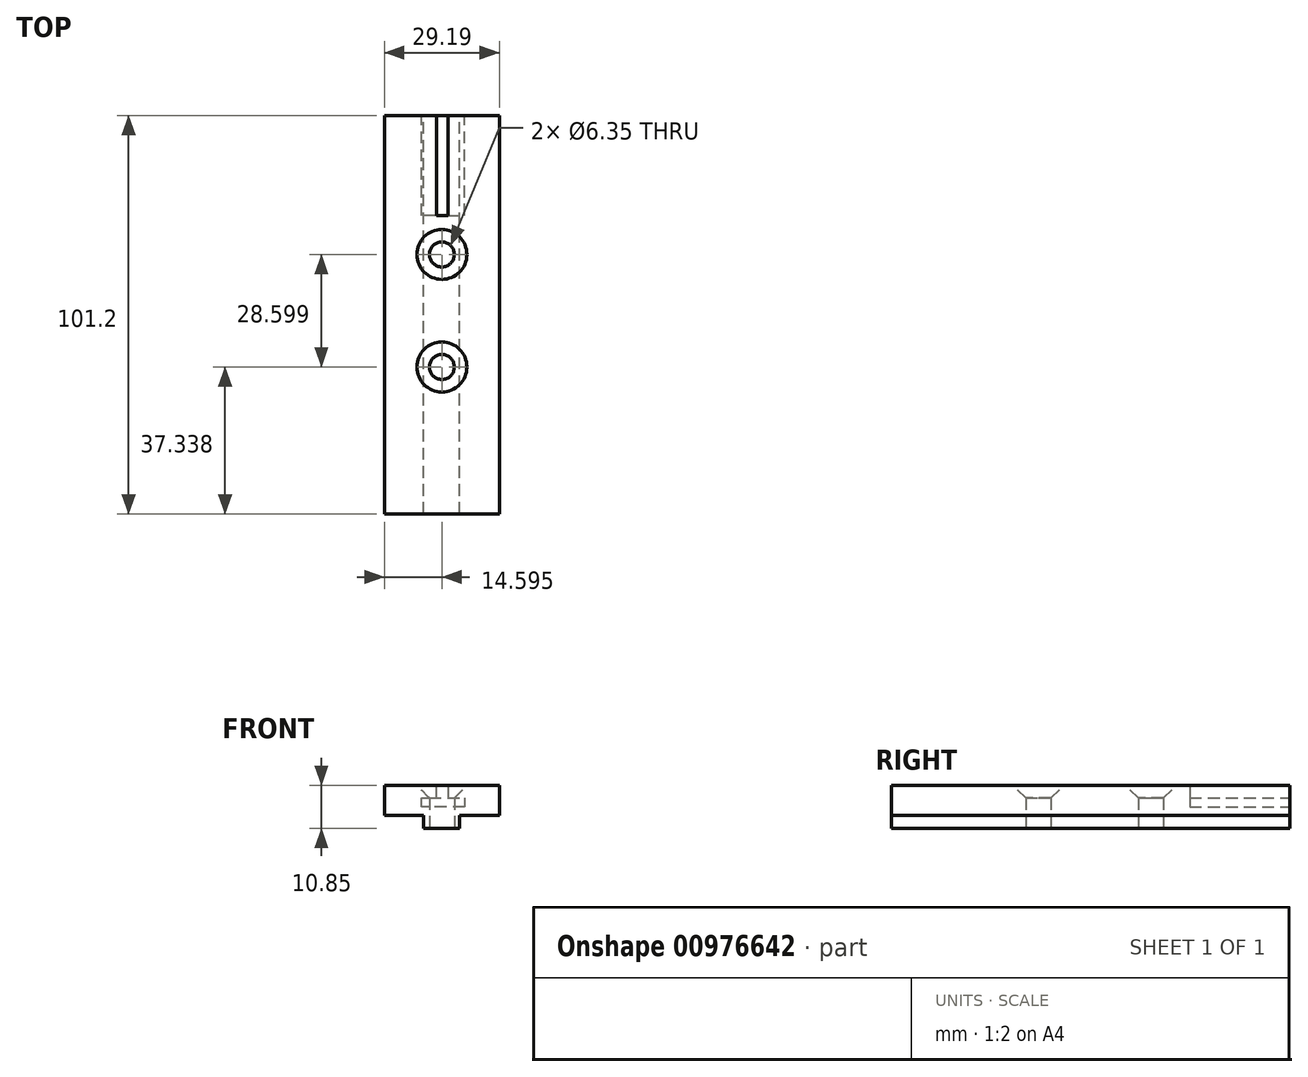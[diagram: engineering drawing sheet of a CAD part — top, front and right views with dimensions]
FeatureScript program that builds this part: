
annotation { "Feature Type Name" : "Feature", "Feature Type Description" : "" }
export const myFeature = defineFeature(function(context is Context, id is Id, definition is map)
    precondition{}
    {
        {
            var Q0;
            Q0=qCreatedBy(makeId("Front.planeOp"),FACE);
            var sketch = newSketch(context, id + "F0", { "sketchPlane" : qUnion([Q0])});
            skLineSegment(sketch, "E0", {"start": v(-1.19, 0) * mm, "end": v(29.2, 0) * mm});
            skLineSegment(sketch, "E1", {"start": v(29.2, 0) * mm, "end": v(29.2, -7.58) * mm});
            skLineSegment(sketch, "E2", {"start": v(29.2, -7.58) * mm, "end": v(18.01, -7.58) * mm});
            skLineSegment(sketch, "E3", {"start": v(18.01, -7.58) * mm, "end": v(18.01, -10.85) * mm});
            skLineSegment(sketch, "E4", {"start": v(18.01, -10.85) * mm, "end": v(12.2, -10.85) * mm});
            skLineSegment(sketch, "E5", {"start": v(12.2, -10.85) * mm, "end": v(12.2, -7.58) * mm});
            skLineSegment(sketch, "E6", {"start": v(12.2, -7.58) * mm, "end": v(0, -7.58) * mm});
            skLineSegment(sketch, "E7", {"start": v(0, -7.58) * mm, "end": v(0, 0) * mm});
            skSolve(sketch);
        }
        {
            var Q0;
            {var subQ0=sQuery(id+"F0.wireOp",EDGE,"E1");Q0=makeQuery(id+"F0.imprint","IMPRINT",FACE,{"disambiguationData":[TD([[makeQuery(id+"F0.imprint","IMPRINT",EDGE,{"derivedFrom":subQ0}),-1.0]])]});}
            extrude(context, id + "F1", {"entities" : qUnion([Q0]), "depth" : 25 * mm, "offsetDistance" : 25.4 * mm});
        }
        {
            var Q0;
            Q0=makeQuery(id+"F1.opExtrude","SWEPT_FACE",FACE,{"disambiguationData":[OSD([sQuery(id+"F0.wireOp",EDGE,"E5")])]});
            extrude(context, id + "F2", {"entities" : qUnion([Q0]), "operationType" : NewBodyOperationType.ADD, "depth" : 2.18 * mm, "offsetDistance" : 25.4 * mm});
        }
        {
            var Q0;
            {var subQ0=sQuery(id+"F0.wireOp",EDGE,"E5");Q0=makeQuery(id+"F2.boolean.opBoolean","MERGE",FACE,{"derivedFrom":[makeQuery(id+"F1.opExtrude","CAP_FACE",FACE,{"disambiguationData":[OSD([sQuery(id+"F0.wireOp",EDGE,"E0"),sQuery(id+"F0.wireOp",EDGE,"E1"),sQuery(id+"F0.wireOp",EDGE,"E2"),sQuery(id+"F0.wireOp",EDGE,"E3"),sQuery(id+"F0.wireOp",EDGE,"E4"),subQ0,sQuery(id+"F0.wireOp",EDGE,"E6"),sQuery(id+"F0.wireOp",EDGE,"E7")])],"isStart":true}),makeQuery(id+"F2.opExtrude","SWEPT_FACE",FACE,{"disambiguationData":[OSD([subQ0]),TDD([makeQuery(id+"F1.opExtrude","CAP_EDGE",EDGE,{"disambiguationData":[OSD([subQ0])],"isStart":true})])]})]});}
            extrude(context, id + "F3", {"entities" : qUnion([Q0]), "operationType" : NewBodyOperationType.ADD, "depth" : 25.4 * mm, "offsetDistance" : 25.4 * mm});
        }
        {
            var Q0;
            {var subQ0=sQuery(id+"F0.wireOp",EDGE,"E0");Q0=makeQuery(id+"F3.boolean.opBoolean","MERGE",FACE,{"derivedFrom":[makeQuery(id+"F1.opExtrude","SWEPT_FACE",FACE,{"disambiguationData":[OSD([subQ0])]}),makeQuery(id+"F3.opExtrude","SWEPT_FACE",FACE,{"disambiguationData":[OSD([subQ0])]})]});}
            var sketch = newSketch(context, id + "F4", { "sketchPlane" : qUnion([Q0])});
            skLineSegment(sketch, "E8", {"start": v(14.6, 25.4) * mm, "end": v(14.6, -25) * mm, "construction": true});
            skPoint(sketch, "E9", {"position": v(14.6, 15.54) * mm});
            skPoint(sketch, "E10", {"position": v(14.6, -13.06) * mm});
            skSolve(sketch);
        }
        {
            var Q0;
            Q0=sQuery(id+"F4.wireOp",VERTEX,"E9");
            var Q1;
            Q1=sQuery(id+"F4.wireOp",VERTEX,"E10");
            var Q2;
            Q2=makeQuery(id+"F1.opExtrude","SWEPT_BODY",BODY,{"disambiguationData":[OSD([sQuery(id+"F0.wireOp",EDGE,"E0"),sQuery(id+"F0.wireOp",EDGE,"E1"),sQuery(id+"F0.wireOp",EDGE,"E2"),sQuery(id+"F0.wireOp",EDGE,"E3"),sQuery(id+"F0.wireOp",EDGE,"E4"),sQuery(id+"F0.wireOp",EDGE,"E5"),sQuery(id+"F0.wireOp",EDGE,"E6"),sQuery(id+"F0.wireOp",EDGE,"E7")])]});
            hole(context, id + "F5", {"style" : HoleStyle.C_SINK, "endStyle" : HoleEndStyle.THROUGH, "holeDiameter" : 6.35 * mm, "cSinkDiameter" : 12.7 * mm, "cSinkAngle" : 90 * degree, "majorDiameter" : 6.35 * mm, "isTappedThrough" : true, "tappedDepth" : 12.7 * mm, "tapClearance" : 3, "locations" : qUnion([Q0, Q1]), "scope" : qUnion([Q2])});
        }
        {
            var Q0;
            {var subQ0=sQuery(id+"F0.wireOp",EDGE,"E3");Q0=makeQuery(id+"F3.boolean.opBoolean","MERGE",FACE,{"derivedFrom":[makeQuery(id+"F1.opExtrude","SWEPT_FACE",FACE,{"disambiguationData":[OSD([subQ0])]}),makeQuery(id+"F3.opExtrude","SWEPT_FACE",FACE,{"disambiguationData":[OSD([subQ0])]})]});}
            extrude(context, id + "F6", {"entities" : qUnion([Q0]), "operationType" : NewBodyOperationType.ADD, "depth" : 5.08 * mm, "offsetDistance" : 25.4 * mm});
        }
        {
            var Q0;
            {var subQ0=sQuery(id+"F0.wireOp",EDGE,"E3");var subQ1=sQuery(id+"F0.wireOp",EDGE,"E5");Q0=makeQuery(id+"F6.boolean.opBoolean","MERGE",FACE,{"derivedFrom":[makeQuery(id+"F2.boolean.opBoolean","MERGE",FACE,{"derivedFrom":[makeQuery(id+"F1.opExtrude","CAP_FACE",FACE,{"disambiguationData":[OSD([sQuery(id+"F0.wireOp",EDGE,"E0"),sQuery(id+"F0.wireOp",EDGE,"E1"),sQuery(id+"F0.wireOp",EDGE,"E2"),subQ0,sQuery(id+"F0.wireOp",EDGE,"E4"),subQ1,sQuery(id+"F0.wireOp",EDGE,"E6"),sQuery(id+"F0.wireOp",EDGE,"E7")])],"isStart":false}),makeQuery(id+"F2.opExtrude","SWEPT_FACE",FACE,{"disambiguationData":[OSD([subQ1]),TDD([makeQuery(id+"F1.opExtrude","CAP_EDGE",EDGE,{"disambiguationData":[OSD([subQ1])],"isStart":false})])]})]}),makeQuery(id+"F6.opExtrude","SWEPT_FACE",FACE,{"disambiguationData":[OSD([subQ0]),TDD([makeQuery(id+"F1.opExtrude","CAP_EDGE",EDGE,{"disambiguationData":[OSD([subQ0])],"isStart":false})])]})]});}
            extrude(context, id + "F7", {"entities" : qUnion([Q0]), "operationType" : NewBodyOperationType.ADD, "depth" : 25.4 * mm, "offsetDistance" : 25.4 * mm});
        }
        {
            var Q0;
            {var subQ0=sQuery(id+"F0.wireOp",EDGE,"E3");Q0=makeQuery(id+"F6.boolean.opBoolean","MERGE",FACE,{"derivedFrom":[makeQuery(id+"F3.opExtrude","CAP_FACE",FACE,{"disambiguationData":[OSD([sQuery(id+"F0.wireOp",EDGE,"E0"),sQuery(id+"F0.wireOp",EDGE,"E1"),sQuery(id+"F0.wireOp",EDGE,"E2"),subQ0,sQuery(id+"F0.wireOp",EDGE,"E4"),sQuery(id+"F0.wireOp",EDGE,"E5"),sQuery(id+"F0.wireOp",EDGE,"E6"),sQuery(id+"F0.wireOp",EDGE,"E7")])],"isStart":false}),makeQuery(id+"F6.opExtrude","SWEPT_FACE",FACE,{"disambiguationData":[OSD([subQ0]),TDD([makeQuery(id+"F3.opExtrude","CAP_EDGE",EDGE,{"disambiguationData":[OSD([subQ0])],"isStart":false})])]})]});}
            extrude(context, id + "F8", {"entities" : qUnion([Q0]), "operationType" : NewBodyOperationType.ADD, "depth" : 25.4 * mm, "offsetDistance" : 25.4 * mm});
        }
        {
            var Q0;
            {var subQ0=sQuery(id+"F0.wireOp",EDGE,"E3");Q0=makeQuery(id+"F8.boolean.opBoolean","MERGE",FACE,{"derivedFrom":[makeQuery(id+"F7.boolean.opBoolean","MERGE",FACE,{"derivedFrom":[makeQuery(id+"F6.opExtrude","CAP_FACE",FACE,{"disambiguationData":[OSD([subQ0])],"isStart":false}),makeQuery(id+"F7.opExtrude","SWEPT_FACE",FACE,{"disambiguationData":[OSD([subQ0])]})]}),makeQuery(id+"F8.opExtrude","SWEPT_FACE",FACE,{"disambiguationData":[OSD([subQ0])]})]});}
            extrude(context, id + "F9", {"entities" : qUnion([Q0]), "operationType" : NewBodyOperationType.REMOVE, "oppositeDirection" : true, "depth" : 4.06 * mm, "offsetDistance" : 25.4 * mm});
        }
        {
            var Q0;
            Q0=makeQuery(id+"F8.opExtrude","CAP_FACE",FACE,{"disambiguationData":[OSD([sQuery(id+"F0.wireOp",EDGE,"E0"),sQuery(id+"F0.wireOp",EDGE,"E1"),sQuery(id+"F0.wireOp",EDGE,"E2"),sQuery(id+"F0.wireOp",EDGE,"E3"),sQuery(id+"F0.wireOp",EDGE,"E4"),sQuery(id+"F0.wireOp",EDGE,"E5"),sQuery(id+"F0.wireOp",EDGE,"E6"),sQuery(id+"F0.wireOp",EDGE,"E7")])],"isStart":false});
            var sketch = newSketch(context, id + "F10", { "sketchPlane" : qUnion([Q0])});
            skLineSegment(sketch, "E11", {"start": v(-14.6, 0) * mm, "end": v(-14.6, -13.57) * mm, "construction": true});
            skLineSegment(sketch, "E12", {"start": v(-16.14, 0) * mm, "end": v(-16.14, -3.19) * mm});
            skLineSegment(sketch, "E13", {"start": v(-16.14, -3.19) * mm, "end": v(-20.4, -3.19) * mm});
            skLineSegment(sketch, "E14", {"start": v(-20.4, -3.19) * mm, "end": v(-20.4, -5.4) * mm});
            skLineSegment(sketch, "E15", {"start": v(-20.4, -5.4) * mm, "end": v(-9.44, -5.4) * mm});
            skLineSegment(sketch, "E16", {"start": v(-9.44, -5.4) * mm, "end": v(-9.44, -3.19) * mm});
            skLineSegment(sketch, "E17", {"start": v(-9.44, -3.19) * mm, "end": v(-13.2, -3.19) * mm});
            skLineSegment(sketch, "E18", {"start": v(-13.2, -3.19) * mm, "end": v(-13.2, 0) * mm});
            skLineSegment(sketch, "E19", {"start": v(-13.2, 0) * mm, "end": v(-16.14, 0) * mm});
            skSolve(sketch);
        }
        {
            var Q0;
            Q0 = qSketchRegion(id + "F10", true);
            extrude(context, id + "F11", {"entities" : qUnion([Q0]), "operationType" : NewBodyOperationType.REMOVE, "oppositeDirection" : true, "depth" : 25.4 * mm, "offsetDistance" : 25.4 * mm});
        }
    });
